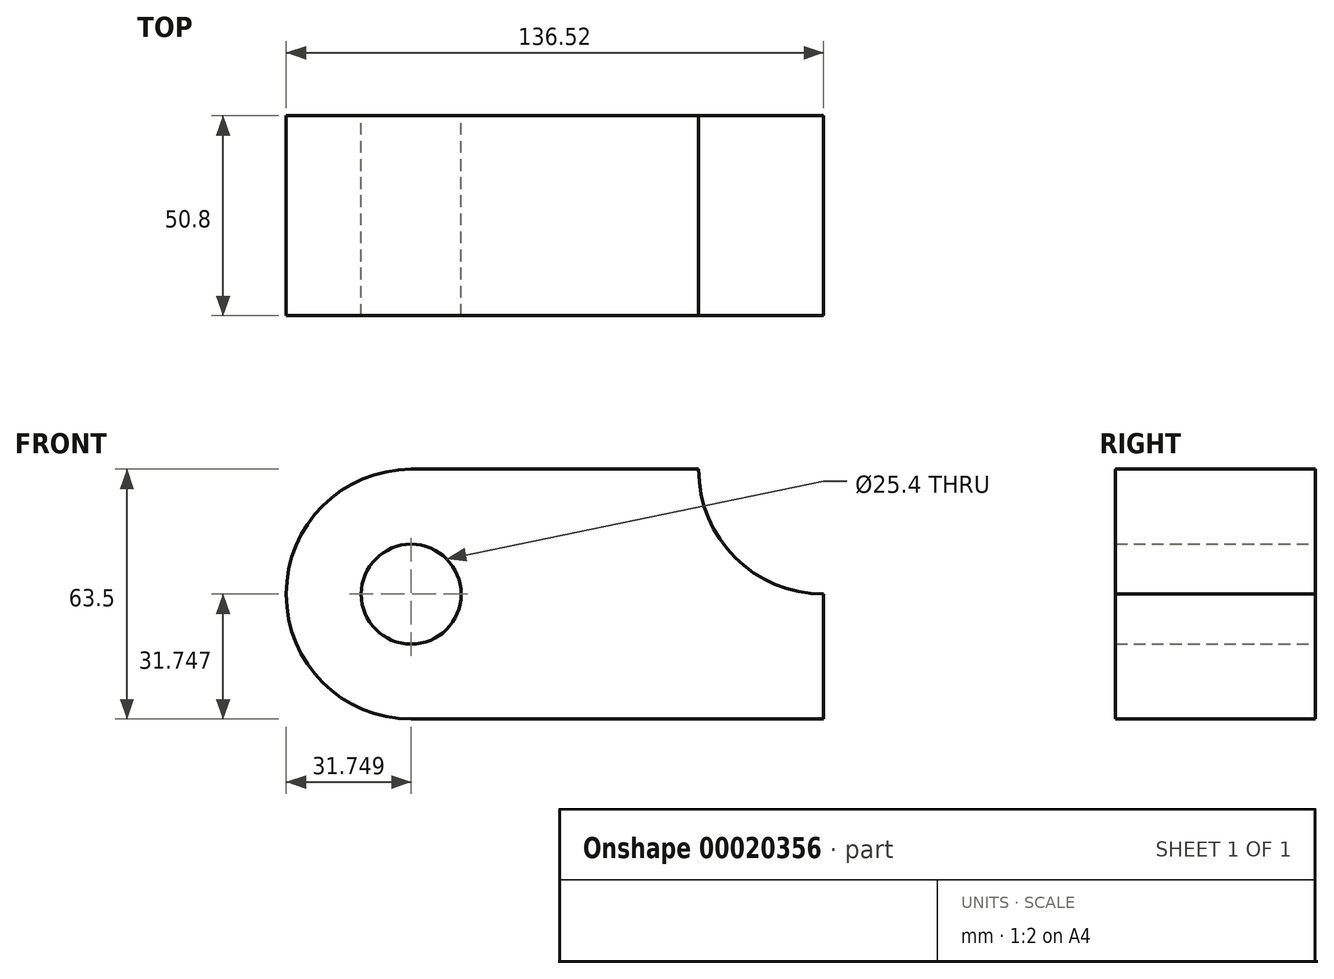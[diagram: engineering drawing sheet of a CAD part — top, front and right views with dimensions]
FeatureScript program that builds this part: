
annotation { "Feature Type Name" : "Feature", "Feature Type Description" : "" }
export const myFeature = defineFeature(function(context is Context, id is Id, definition is map)
    precondition{}
    {
        {
            var Q0;
            Q0=qCreatedBy(makeId("Front.planeOp"),FACE);
            var sketch = newSketch(context, id + "F0", { "sketchPlane" : qUnion([Q0])});
            skLineSegment(sketch, "E0.bottom", {"start": v(-44.68, 26.9) * mm, "end": v(60.1, 26.9) * mm});
            skLineSegment(sketch, "E0.top", {"start": v(-44.68, -36.6) * mm, "end": v(60.1, -36.6) * mm});
            skLineSegment(sketch, "E0.left", {"start": v(-44.68, 26.9) * mm, "end": v(-44.68, -36.6) * mm});
            skLineSegment(sketch, "E0.right", {"start": v(60.1, 26.9) * mm, "end": v(60.1, -36.6) * mm});
            skCircle(sketch, "E1", {"center": v(-44.68, -4.84) * mm, "radius": 31.75 * mm});
            skCircle(sketch, "E2", {"center": v(-44.68, -4.84) * mm, "radius": 12.7 * mm});
            skCircle(sketch, "E3", {"center": v(60.1, 26.9) * mm, "radius": 31.75 * mm});
            skSolve(sketch);
        }
        {
            var Q0;
            {var subQ6=sQuery(id+"F0.wireOp",EDGE,"E0.top");Q0=makeQuery(id+"F0.imprint","IMPRINT",FACE,{"disambiguationData":[TD([[makeQuery(id+"F0.imprint","IMPRINT",EDGE,{"derivedFrom":subQ6}),1.0]])]});}
            var Q1;
            {var subQ0=sQuery(id+"F0.wireOp",EDGE,"E2");var subQ1=sQuery(id+"F0.wireOp",EDGE,"E0.left");var subQ3=makeQuery(id+"F0.imprint","INTERSECT",VERTEX,{"disambiguationData":[OD(0.0)],"derivedFrom":[subQ1,subQ0]});Q1=makeQuery(id+"F0.imprint","IMPRINT",FACE,{"disambiguationData":[TD([[makeQuery(id+"F0.imprint","IMPRINT",EDGE,{"disambiguationData":[TD([[subQ3,-1.0]])],"derivedFrom":subQ0}),-1.0]])]});}
            var Q2;
            {var subQ0=sQuery(id+"F0.wireOp",EDGE,"E2");var subQ1=sQuery(id+"F0.wireOp",EDGE,"E0.left");var subQ3=makeQuery(id+"F0.imprint","INTERSECT",VERTEX,{"disambiguationData":[OD(0.0)],"derivedFrom":[subQ1,subQ0]});Q2=makeQuery(id+"F0.imprint","IMPRINT",FACE,{"disambiguationData":[TD([[makeQuery(id+"F0.imprint","IMPRINT",EDGE,{"disambiguationData":[TD([[subQ3,1.0]])],"derivedFrom":subQ0}),-1.0]])]});}
            extrude(context, id + "F1", {"entities" : qUnion([Q0, Q1, Q2]), "depth" : 50.8 * mm});
        }
    });
